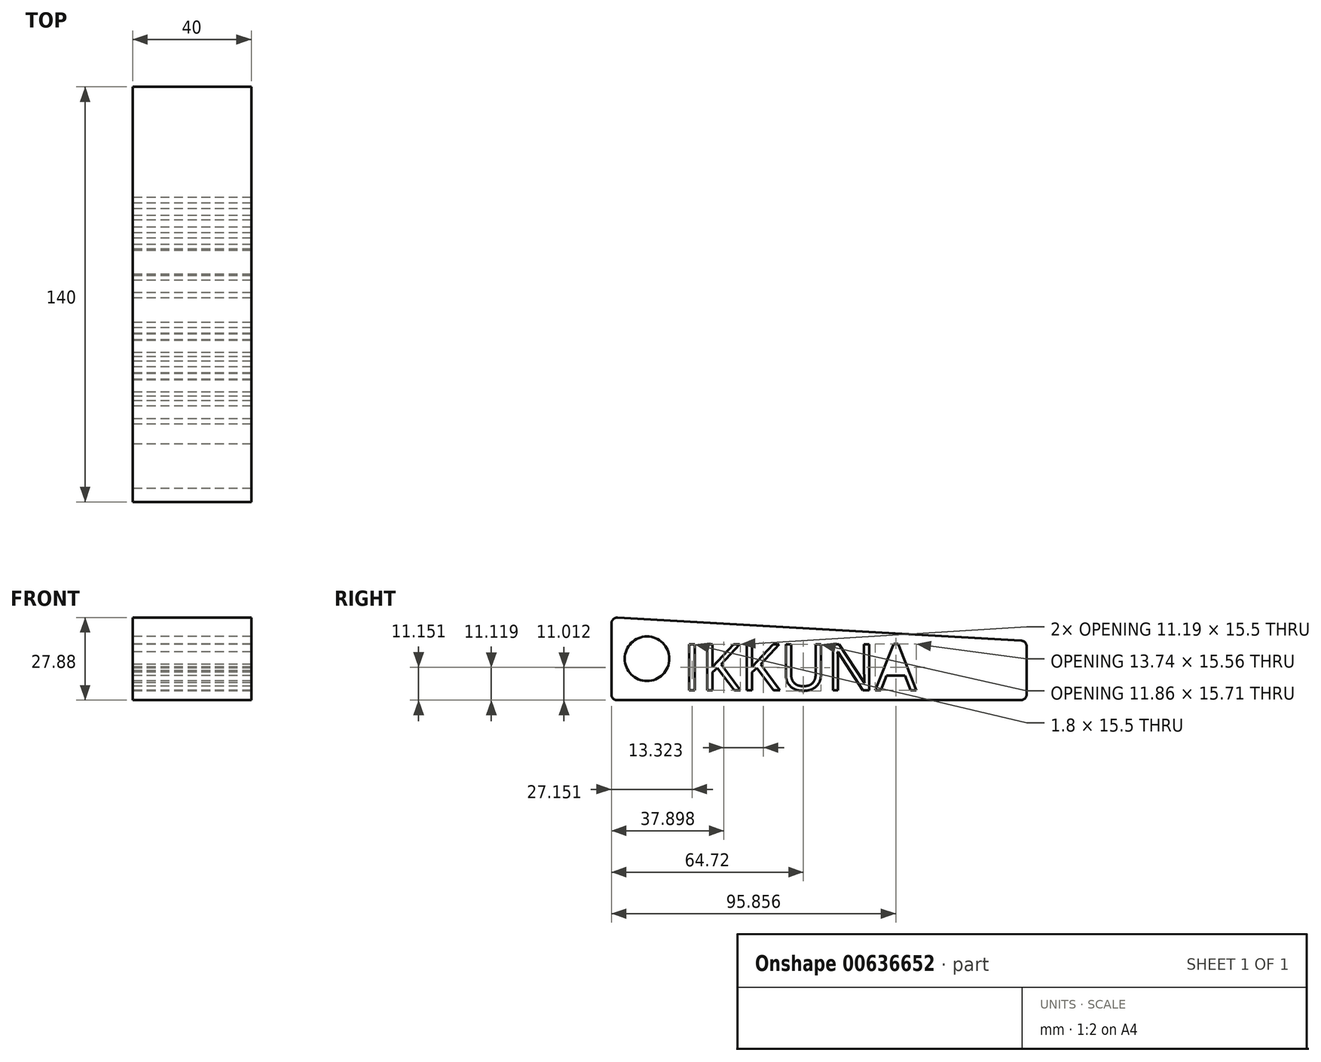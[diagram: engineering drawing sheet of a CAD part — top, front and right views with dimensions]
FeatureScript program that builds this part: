
annotation { "Feature Type Name" : "Feature", "Feature Type Description" : "" }
export const myFeature = defineFeature(function(context is Context, id is Id, definition is map)
    precondition{}
    {
        {
            var Q0;
            Q0=qCreatedBy(makeId("Right.planeOp"),FACE);
            var sketch = newSketch(context, id + "F0", { "sketchPlane" : qUnion([Q0])});
            skLineSegment(sketch, "E0", {"start": v(0, 0) * mm, "end": v(0, 28) * mm});
            skLineSegment(sketch, "E1", {"start": v(0, 28) * mm, "end": v(140, 20) * mm});
            skLineSegment(sketch, "E2", {"start": v(140, 20) * mm, "end": v(140, 0) * mm});
            skLineSegment(sketch, "E3", {"start": v(140, 0) * mm, "end": v(0, 0) * mm});
            skCircle(sketch, "E4", {"center": v(12, 14) * mm, "radius": 7.5 * mm});
            skLineSegment(sketch, "E5", {"start": v(0, 14) * mm, "end": v(12, 14) * mm});
            skText(sketch, "E6", { "text": "IKKUNA", "fontName": "OpenSans-Regular.ttf"});
            const initialGuessF0  = {"E6": [0.02412, 0.00337, 1, 0, 0.01563]};
            skSetInitialGuess(sketch, initialGuessF0);
            skSolve(sketch);
        }
        {
            var Q0;
            Q0 = qSketchRegion(id + "F0", true);
            extrude(context, id + "F1", {"entities" : qUnion([Q0]), "depth" : 40 * mm, "offsetDistance" : 25 * mm});
        }
        {
            var Q0;
            Q0=makeQuery(id+"F1.opExtrude","SWEPT_EDGE",EDGE,{"disambiguationData":[OSD([sQuery(id+"F0.wireOp",EDGE,"E1"),sQuery(id+"F0.wireOp",EDGE,"E2")])]});
            var Q1;
            Q1=makeQuery(id+"F1.opExtrude","SWEPT_EDGE",EDGE,{"disambiguationData":[OSD([sQuery(id+"F0.wireOp",EDGE,"E0"),sQuery(id+"F0.wireOp",EDGE,"E1")])]});
            var Q2;
            Q2=makeQuery(id+"F1.opExtrude","SWEPT_EDGE",EDGE,{"disambiguationData":[OSD([sQuery(id+"F0.wireOp",EDGE,"E0"),sQuery(id+"F0.wireOp",EDGE,"E3")])]});
            var Q3;
            Q3=makeQuery(id+"F1.opExtrude","SWEPT_EDGE",EDGE,{"disambiguationData":[OSD([sQuery(id+"F0.wireOp",EDGE,"E2"),sQuery(id+"F0.wireOp",EDGE,"E3")])]});
            fillet(context, id + "F2", {"entities" : qUnion([Q0, Q1, Q2, Q3]), "radius" : 2 * mm, "tangentPropagation" : true, "allowEdgeOverflow" : false});
        }
    });
